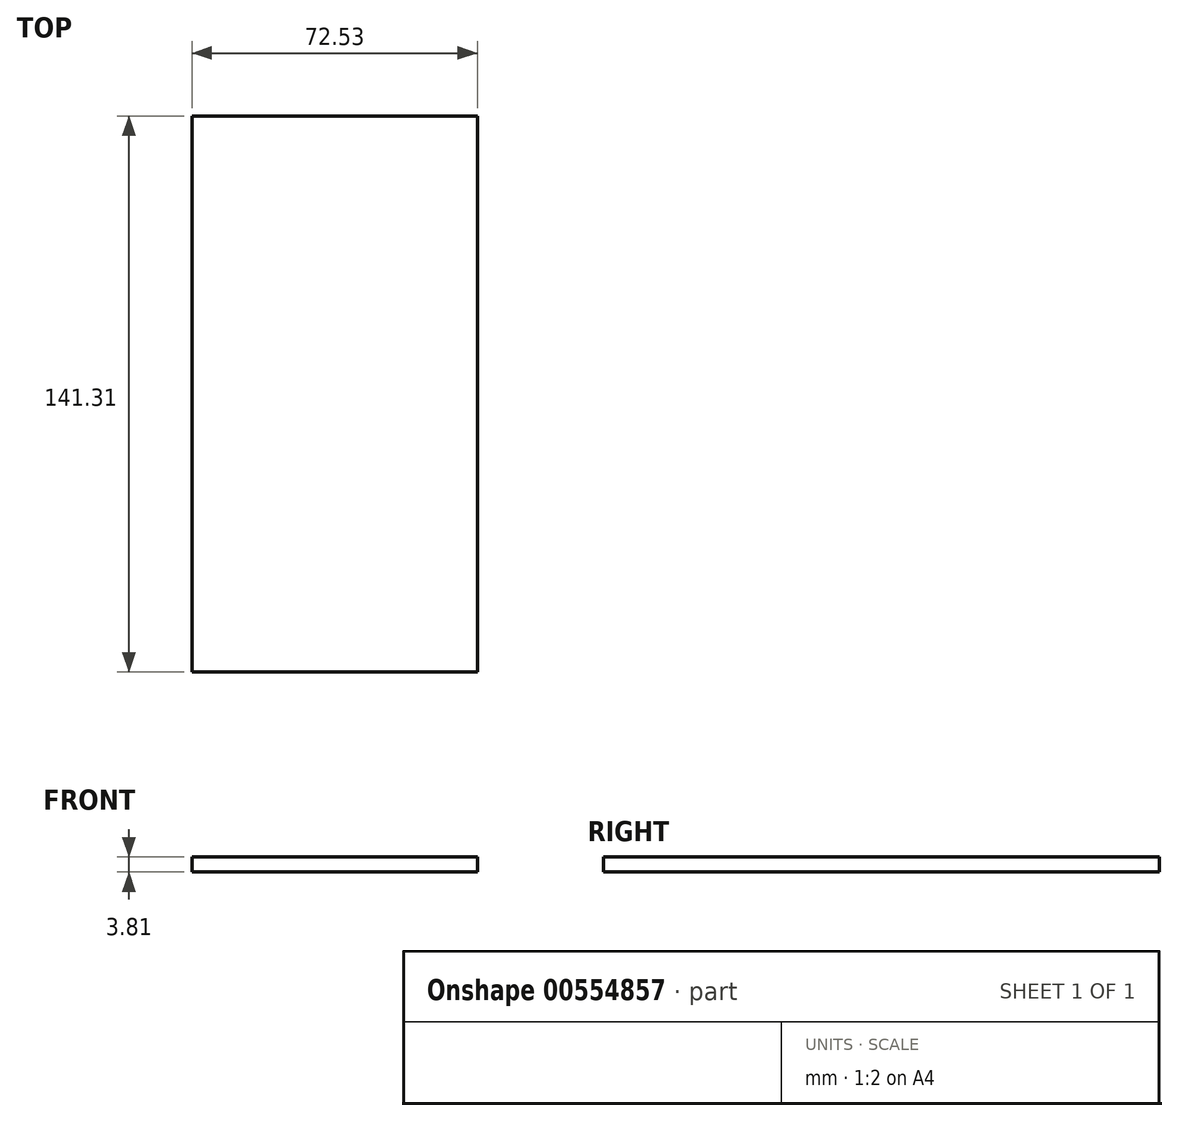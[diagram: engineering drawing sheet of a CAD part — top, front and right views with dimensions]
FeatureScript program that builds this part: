
annotation { "Feature Type Name" : "Feature", "Feature Type Description" : "" }
export const myFeature = defineFeature(function(context is Context, id is Id, definition is map)
    precondition{}
    {
        {
            var Q0;
            Q0=qCreatedBy(makeId("Top.planeOp"),FACE);
            var sketch = newSketch(context, id + "F0", { "sketchPlane" : qUnion([Q0])});
            skLineSegment(sketch, "E0.bottom", {"start": v(-35.4, -69.07) * mm, "end": v(37.13, -69.07) * mm});
            skLineSegment(sketch, "E0.top", {"start": v(-35.4, 72.24) * mm, "end": v(37.13, 72.24) * mm});
            skLineSegment(sketch, "E0.left", {"start": v(-35.4, -69.07) * mm, "end": v(-35.4, 72.24) * mm});
            skLineSegment(sketch, "E0.right", {"start": v(37.13, -69.07) * mm, "end": v(37.13, 72.24) * mm});
            skSolve(sketch);
        }
        {
            var Q0;
            Q0 = qSketchRegion(id + "F0", true);
            extrude(context, id + "F1", {"entities" : qUnion([Q0]), "depth" : 3.8 * mm, "offsetDistance" : 25.4 * mm});
        }
    });
